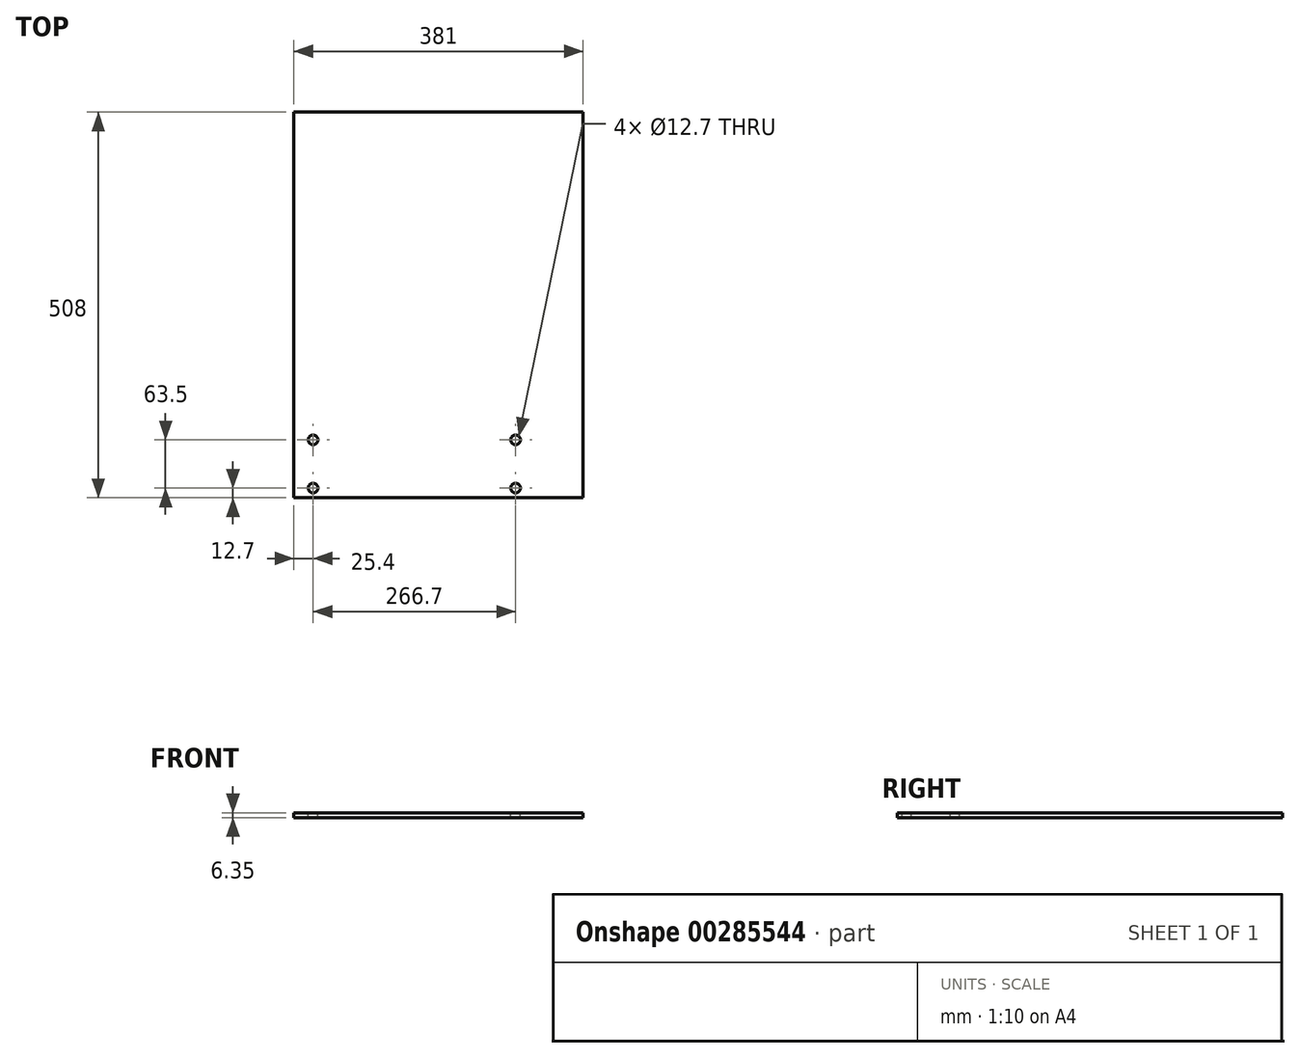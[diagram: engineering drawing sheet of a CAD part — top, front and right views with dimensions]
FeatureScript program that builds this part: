
annotation { "Feature Type Name" : "Feature", "Feature Type Description" : "" }
export const myFeature = defineFeature(function(context is Context, id is Id, definition is map)
    precondition{}
    {
        {
            var Q0;
            Q0=qCreatedBy(makeId("Top.planeOp"),FACE);
            var sketch = newSketch(context, id + "F0", { "sketchPlane" : qUnion([Q0])});
            skLineSegment(sketch, "E0", {"start": v(0, 0) * mm, "end": v(0, 508) * mm});
            skLineSegment(sketch, "E1", {"start": v(0, 508) * mm, "end": v(381, 508) * mm});
            skLineSegment(sketch, "E2", {"start": v(381, 508) * mm, "end": v(381, 0) * mm});
            skLineSegment(sketch, "E3", {"start": v(381, 0) * mm, "end": v(0, 0) * mm});
            skSolve(sketch);
        }
        {
            var Q0;
            Q0 = qSketchRegion(id + "F0", true);
            extrude(context, id + "F1", {"entities" : qUnion([Q0]), "depth" : 6.35 * mm});
        }
        {
            var Q0;
            Q0=makeQuery(id+"F1.opExtrude","CAP_FACE",FACE,{"disambiguationData":[OSD([sQuery(id+"F0.wireOp",EDGE,"E0"),sQuery(id+"F0.wireOp",EDGE,"E1"),sQuery(id+"F0.wireOp",EDGE,"E2"),sQuery(id+"F0.wireOp",EDGE,"E3")])],"isStart":false});
            var sketch = newSketch(context, id + "F2", { "sketchPlane" : qUnion([Q0])});
            skPoint(sketch, "E4", {"position": v(25.4, 12.7) * mm});
            skPoint(sketch, "E5", {"position": v(25.4, 76.2) * mm});
            skPoint(sketch, "E6", {"position": v(292.1, 76.2) * mm});
            skPoint(sketch, "E7", {"position": v(292.1, 12.7) * mm});
            skSolve(sketch);
        }
        {
            var Q0;
            Q0=sQuery(id+"F2.wireOp",VERTEX,"E4");
            var Q1;
            Q1=sQuery(id+"F2.wireOp",VERTEX,"E5");
            var Q2;
            Q2=sQuery(id+"F2.wireOp",VERTEX,"E6");
            var Q3;
            Q3=sQuery(id+"F2.wireOp",VERTEX,"E7");
            var Q4;
            Q4=makeQuery(id+"F1.opExtrude","SWEPT_BODY",BODY,{"disambiguationData":[OSD([sQuery(id+"F0.wireOp",EDGE,"E0"),sQuery(id+"F0.wireOp",EDGE,"E1"),sQuery(id+"F0.wireOp",EDGE,"E2"),sQuery(id+"F0.wireOp",EDGE,"E3")])]});
            hole(context, id + "F3", {"style" : HoleStyle.SIMPLE, "endStyle" : HoleEndStyle.BLIND, "holeDiameter" : 12.7 * mm, "holeDepth" : 25.4 * mm, "tappedDepth" : 12.7 * mm, "tapClearance" : 3, "locations" : qUnion([Q0, Q1, Q2, Q3]), "scope" : qUnion([Q4])});
        }
    });
